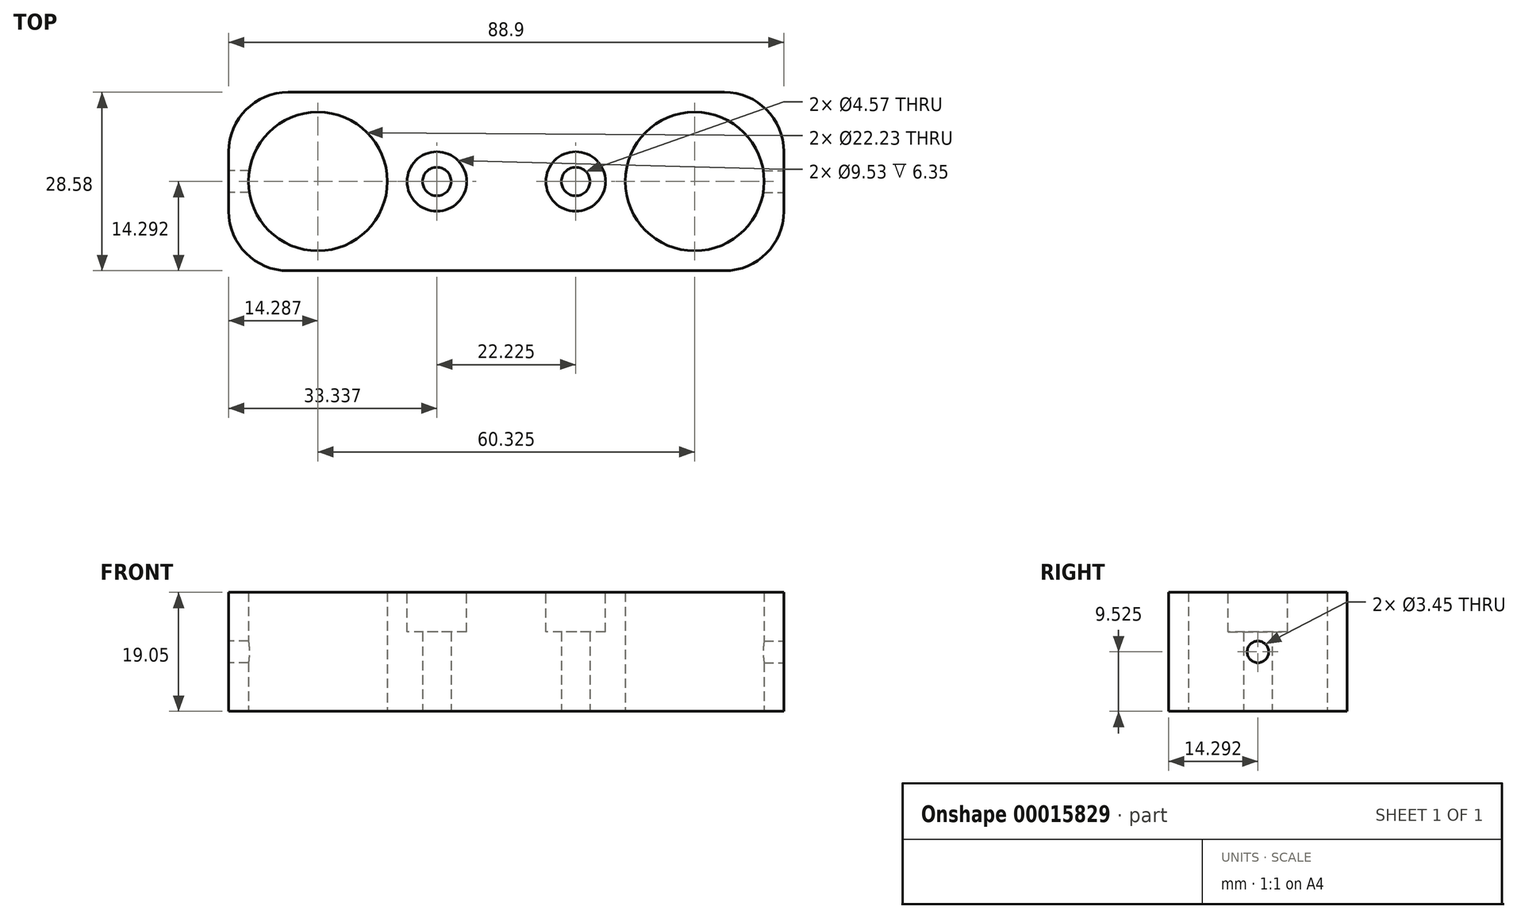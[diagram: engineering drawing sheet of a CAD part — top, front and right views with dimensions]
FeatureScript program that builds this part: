
annotation { "Feature Type Name" : "Feature", "Feature Type Description" : "" }
export const myFeature = defineFeature(function(context is Context, id is Id, definition is map)
    precondition{}
    {
        {
            var Q0;
            Q0=qCreatedBy(makeId("Top.planeOp"),FACE);
            var sketch = newSketch(context, id + "F0", { "sketchPlane" : qUnion([Q0])});
            skLineSegment(sketch, "E0.bottom", {"start": v(0, 0) * mm, "end": v(88.9, 0) * mm});
            skLineSegment(sketch, "E0.top", {"start": v(0, -28.57) * mm, "end": v(88.9, -28.57) * mm});
            skLineSegment(sketch, "E0.left", {"start": v(0, 0) * mm, "end": v(0, -28.57) * mm});
            skLineSegment(sketch, "E0.right", {"start": v(88.9, 0) * mm, "end": v(88.9, -28.57) * mm});
            skLineSegment(sketch, "E1", {"start": v(0, -14.29) * mm, "end": v(14.29, -14.29) * mm});
            skLineSegment(sketch, "E2", {"start": v(88.9, -14.29) * mm, "end": v(74.61, -14.29) * mm});
            skCircle(sketch, "E3", {"center": v(14.29, -14.29) * mm, "radius": 11.11 * mm});
            skCircle(sketch, "E4", {"center": v(74.61, -14.29) * mm, "radius": 11.11 * mm});
            skLineSegment(sketch, "E5", {"start": v(44.45, 0) * mm, "end": v(44.45, -28.57) * mm});
            skPoint(sketch, "E6", {"position": v(44.45, -14.29) * mm});
            skLineSegment(sketch, "E7", {"start": v(33.34, -14.29) * mm, "end": v(55.56, -14.29) * mm});
            skCircle(sketch, "E8", {"center": v(33.34, -14.29) * mm, "radius": 2.29 * mm});
            skCircle(sketch, "E9", {"center": v(55.56, -14.29) * mm, "radius": 2.29 * mm});
            skSolve(sketch);
        }
        {
            var Q0;
            Q0 = qSketchRegion(id + "F0", true);
            extrude(context, id + "F1", {"entities" : qUnion([Q0]), "depth" : 19.05 * mm});
        }
        {
            var Q0;
            Q0=makeQuery(id+"F1.opExtrude","CAP_FACE",FACE,{"disambiguationData":[OSD([sQuery(id+"F0.wireOp",EDGE,"E0.bottom"),sQuery(id+"F0.wireOp",EDGE,"E0.top"),sQuery(id+"F0.wireOp",EDGE,"E0.left"),sQuery(id+"F0.wireOp",EDGE,"E0.right"),sQuery(id+"F0.wireOp",EDGE,"E3"),sQuery(id+"F0.wireOp",EDGE,"E4"),sQuery(id+"F0.wireOp",EDGE,"E8"),sQuery(id+"F0.wireOp",EDGE,"E9")])],"isStart":false});
            var sketch = newSketch(context, id + "F2", { "sketchPlane" : qUnion([Q0])});
            skCircle(sketch, "E10", {"center": v(33.34, -14.29) * mm, "radius": 4.76 * mm});
            skCircle(sketch, "E11", {"center": v(55.56, -14.29) * mm, "radius": 4.76 * mm});
            skSolve(sketch);
        }
        {
            var Q0;
            Q0 = qSketchRegion(id + "F2", true);
            extrude(context, id + "F3", {"entities" : qUnion([Q0]), "operationType" : NewBodyOperationType.REMOVE, "oppositeDirection" : true, "depth" : 6.35 * mm});
        }
        {
            var Q0;
            Q0=makeQuery(id+"F1.opExtrude","SWEPT_EDGE",EDGE,{"disambiguationData":[OSD([sQuery(id+"F0.wireOp",EDGE,"E0.top"),sQuery(id+"F0.wireOp",EDGE,"E0.left")])]});
            var Q1;
            Q1=makeQuery(id+"F1.opExtrude","SWEPT_EDGE",EDGE,{"disambiguationData":[OSD([sQuery(id+"F0.wireOp",EDGE,"E0.top"),sQuery(id+"F0.wireOp",EDGE,"E0.right")])]});
            var Q2;
            Q2=makeQuery(id+"F1.opExtrude","SWEPT_EDGE",EDGE,{"disambiguationData":[OSD([sQuery(id+"F0.wireOp",EDGE,"E0.bottom"),sQuery(id+"F0.wireOp",EDGE,"E0.right")])]});
            var Q3;
            Q3=makeQuery(id+"F1.opExtrude","SWEPT_EDGE",EDGE,{"disambiguationData":[OSD([sQuery(id+"F0.wireOp",EDGE,"E0.bottom"),sQuery(id+"F0.wireOp",EDGE,"E0.left")])]});
            fillet(context, id + "F4", {"entities" : qUnion([Q0, Q1, Q2, Q3]), "radius" : 9.52 * mm, "tangentPropagation" : true, "allowEdgeOverflow" : false});
        }
        {
            var Q0;
            Q0=makeQuery(id+"F1.opExtrude","SWEPT_FACE",FACE,{"disambiguationData":[OSD([sQuery(id+"F0.wireOp",EDGE,"E0.left")])]});
            var sketch = newSketch(context, id + "F5", { "sketchPlane" : qUnion([Q0])});
            skLineSegment(sketch, "E12", {"start": v(9.52, 9.53) * mm, "end": v(19.05, 9.53) * mm});
            skCircle(sketch, "E13", {"center": v(14.29, 9.53) * mm, "radius": 1.73 * mm});
            skSolve(sketch);
        }
        {
            var Q0;
            Q0 = qSketchRegion(id + "F5", true);
            var Q1;
            Q1=makeQuery(id+"F1.opExtrude","SWEPT_FACE",FACE,{"disambiguationData":[OSD([sQuery(id+"F0.wireOp",EDGE,"E3")])]});
            extrude(context, id + "F6", {"entities" : qUnion([Q0]), "operationType" : NewBodyOperationType.REMOVE, "endBound" : BoundingType.UP_TO_SURFACE, "oppositeDirection" : true, "endBoundEntityFace" : qUnion([Q1]), "depth" : 25.4 * mm});
        }
        {
            var Q0;
            Q0=makeQuery(id+"F1.opExtrude","SWEPT_FACE",FACE,{"disambiguationData":[OSD([sQuery(id+"F0.wireOp",EDGE,"E0.right")])]});
            var sketch = newSketch(context, id + "F7", { "sketchPlane" : qUnion([Q0])});
            skCircle(sketch, "E14", {"center": v(-14.29, 9.52) * mm, "radius": 1.73 * mm});
            skSolve(sketch);
        }
        {
            var Q0;
            Q0 = qSketchRegion(id + "F7", true);
            var Q1;
            Q1=makeQuery(id+"F1.opExtrude","SWEPT_FACE",FACE,{"disambiguationData":[OSD([sQuery(id+"F0.wireOp",EDGE,"E4")])]});
            extrude(context, id + "F8", {"entities" : qUnion([Q0]), "operationType" : NewBodyOperationType.REMOVE, "endBound" : BoundingType.UP_TO_SURFACE, "oppositeDirection" : true, "endBoundEntityFace" : qUnion([Q1]), "depth" : 25.4 * mm});
        }
    });
